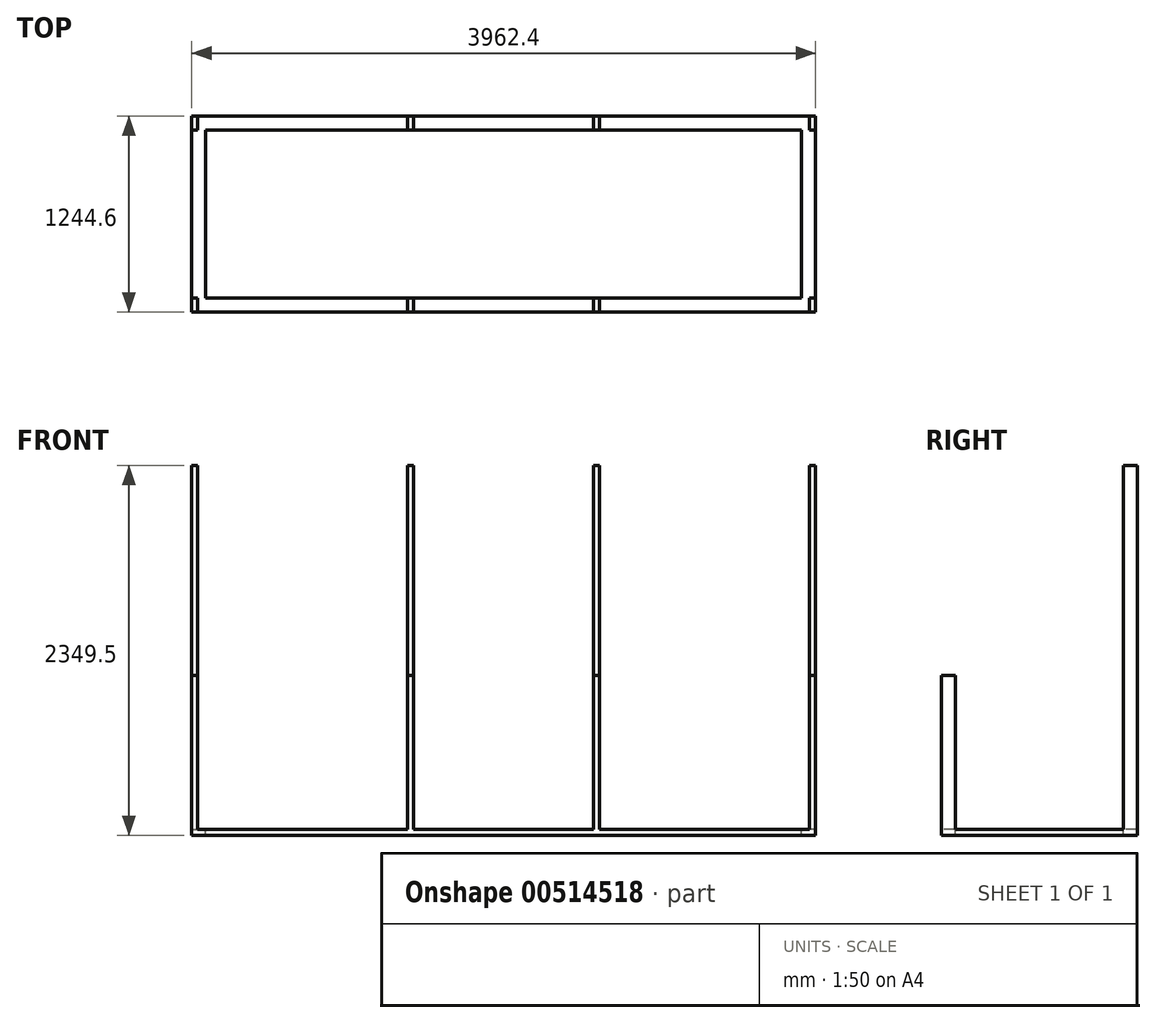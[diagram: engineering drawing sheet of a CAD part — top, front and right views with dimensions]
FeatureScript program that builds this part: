
annotation { "Feature Type Name" : "Feature", "Feature Type Description" : "" }
export const myFeature = defineFeature(function(context is Context, id is Id, definition is map)
    precondition{}
    {
        {
            var Q0;
            Q0=qCreatedBy(makeId("Front.planeOp"),FACE);
            var sketch = newSketch(context, id + "F0", { "sketchPlane" : qUnion([Q0])});
            skLineSegment(sketch, "E0.bottom", {"start": v(0, 0) * mm, "end": v(3962.4, 0) * mm});
            skLineSegment(sketch, "E0.top", {"start": v(0, 38.1) * mm, "end": v(3962.4, 38.1) * mm});
            skLineSegment(sketch, "E0.left", {"start": v(0, 0) * mm, "end": v(0, 38.1) * mm});
            skLineSegment(sketch, "E0.right", {"start": v(3962.4, 0) * mm, "end": v(3962.4, 38.1) * mm});
            skSolve(sketch);
        }
        {
            var Q0;
            Q0=makeQuery(id+"F0.imprint","IMPRINT",FACE,{"disambiguationData":[TD([[makeQuery(id+"F0.imprint","IMPRINT",EDGE,{"derivedFrom":sQuery(id+"F0.wireOp",EDGE,"E0.bottom")}),1.0]])]});
            extrude(context, id + "F1", {"entities" : qUnion([Q0]), "depth" : 88.9 * mm, "offsetDistance" : 25.4 * mm});
        }
        {
            var Q0;
            Q0=makeQuery(id+"F1.opExtrude","SWEPT_FACE",FACE,{"disambiguationData":[OSD([sQuery(id+"F0.wireOp",EDGE,"E0.top")])]});
            var sketch = newSketch(context, id + "F2", { "sketchPlane" : qUnion([Q0])});
            skLineSegment(sketch, "E1.bottom", {"start": v(0, 0) * mm, "end": v(38.1, 0) * mm});
            skLineSegment(sketch, "E1.top", {"start": v(0, -88.9) * mm, "end": v(38.1, -88.9) * mm});
            skLineSegment(sketch, "E1.left", {"start": v(0, 0) * mm, "end": v(0, -88.9) * mm});
            skLineSegment(sketch, "E1.right", {"start": v(38.1, 0) * mm, "end": v(38.1, -88.9) * mm});
            skLineSegment(sketch, "E2.bottom", {"start": v(3962.4, 0) * mm, "end": v(3924.3, 0) * mm});
            skLineSegment(sketch, "E2.top", {"start": v(3962.4, -88.9) * mm, "end": v(3924.3, -88.9) * mm});
            skLineSegment(sketch, "E2.left", {"start": v(3962.4, 0) * mm, "end": v(3962.4, -88.9) * mm});
            skLineSegment(sketch, "E2.right", {"start": v(3924.3, 0) * mm, "end": v(3924.3, -88.9) * mm});
            skLineSegment(sketch, "E3.bottom", {"start": v(2590.8, 0) * mm, "end": v(2552.7, 0) * mm});
            skLineSegment(sketch, "E3.top", {"start": v(2590.8, -88.9) * mm, "end": v(2552.7, -88.9) * mm});
            skLineSegment(sketch, "E3.left", {"start": v(2590.8, 0) * mm, "end": v(2590.8, -88.9) * mm});
            skLineSegment(sketch, "E3.right", {"start": v(2552.7, 0) * mm, "end": v(2552.7, -88.9) * mm});
            skLineSegment(sketch, "E4.bottom", {"start": v(1371.6, 0) * mm, "end": v(1409.7, 0) * mm});
            skLineSegment(sketch, "E4.top", {"start": v(1371.6, -88.9) * mm, "end": v(1409.7, -88.9) * mm});
            skLineSegment(sketch, "E4.left", {"start": v(1371.6, 0) * mm, "end": v(1371.6, -88.9) * mm});
            skLineSegment(sketch, "E4.right", {"start": v(1409.7, 0) * mm, "end": v(1409.7, -88.9) * mm});
            skSolve(sketch);
        }
        {
            var Q0;
            Q0=makeQuery(id+"F2.imprint","IMPRINT",FACE,{"disambiguationData":[TD([[makeQuery(id+"F2.imprint","IMPRINT",EDGE,{"derivedFrom":sQuery(id+"F2.wireOp",EDGE,"E1.bottom")}),-1.0]])]});
            var Q1;
            Q1=makeQuery(id+"F2.imprint","IMPRINT",FACE,{"disambiguationData":[TD([[makeQuery(id+"F2.imprint","IMPRINT",EDGE,{"derivedFrom":sQuery(id+"F2.wireOp",EDGE,"E4.bottom")}),-1.0]])]});
            var Q2;
            Q2=makeQuery(id+"F2.imprint","IMPRINT",FACE,{"disambiguationData":[TD([[makeQuery(id+"F2.imprint","IMPRINT",EDGE,{"derivedFrom":sQuery(id+"F2.wireOp",EDGE,"E3.bottom")}),-1.0]])]});
            var Q3;
            Q3=makeQuery(id+"F2.imprint","IMPRINT",FACE,{"disambiguationData":[TD([[makeQuery(id+"F2.imprint","IMPRINT",EDGE,{"derivedFrom":sQuery(id+"F2.wireOp",EDGE,"E2.bottom")}),-1.0]])]});
            extrude(context, id + "F3", {"entities" : qUnion([Q0, Q1, Q2, Q3]), "operationType" : NewBodyOperationType.ADD, "depth" : 977.9 * mm, "offsetDistance" : 25.4 * mm});
        }
        {
            var Q0;
            Q0=makeQuery(id+"F3.boolean.opBoolean","MERGE",FACE,{"derivedFrom":[makeQuery(id+"F1.opExtrude","CAP_FACE",FACE,{"disambiguationData":[OSD([sQuery(id+"F0.wireOp",EDGE,"E0.bottom"),sQuery(id+"F0.wireOp",EDGE,"E0.top"),sQuery(id+"F0.wireOp",EDGE,"E0.left"),sQuery(id+"F0.wireOp",EDGE,"E0.right")])],"isStart":true}),makeQuery(id+"F3.opExtrude","SWEPT_FACE",FACE,{"disambiguationData":[OSD([sQuery(id+"F2.wireOp",EDGE,"E1.bottom")])]}),makeQuery(id+"F3.opExtrude","SWEPT_FACE",FACE,{"disambiguationData":[OSD([sQuery(id+"F2.wireOp",EDGE,"E2.bottom")])]}),makeQuery(id+"F3.opExtrude","SWEPT_FACE",FACE,{"disambiguationData":[OSD([sQuery(id+"F2.wireOp",EDGE,"E3.bottom")])]}),makeQuery(id+"F3.opExtrude","SWEPT_FACE",FACE,{"disambiguationData":[OSD([sQuery(id+"F2.wireOp",EDGE,"E4.bottom")])]})]});
            var sketch = newSketch(context, id + "F4", { "sketchPlane" : qUnion([Q0])});
            skLineSegment(sketch, "E5.bottom", {"start": v(-3962.4, 0) * mm, "end": v(-3873.5, 0) * mm});
            skLineSegment(sketch, "E5.top", {"start": v(-3962.4, 38.1) * mm, "end": v(-3873.5, 38.1) * mm});
            skLineSegment(sketch, "E5.left", {"start": v(-3962.4, 0) * mm, "end": v(-3962.4, 38.1) * mm});
            skLineSegment(sketch, "E5.right", {"start": v(-3873.5, 0) * mm, "end": v(-3873.5, 38.1) * mm});
            skLineSegment(sketch, "E6.bottom", {"start": v(0, 0) * mm, "end": v(-88.9, 0) * mm});
            skLineSegment(sketch, "E6.top", {"start": v(0, 38.1) * mm, "end": v(-88.9, 38.1) * mm});
            skLineSegment(sketch, "E6.left", {"start": v(0, 0) * mm, "end": v(0, 38.1) * mm});
            skLineSegment(sketch, "E6.right", {"start": v(-88.9, 0) * mm, "end": v(-88.9, 38.1) * mm});
            skSolve(sketch);
        }
        {
            var Q0;
            Q0=makeQuery(id+"F4.imprint","IMPRINT",FACE,{"disambiguationData":[TD([[makeQuery(id+"F4.imprint","IMPRINT",EDGE,{"derivedFrom":sQuery(id+"F4.wireOp",EDGE,"E6.bottom")}),-1.0]])]});
            var Q1;
            Q1=makeQuery(id+"F4.imprint","IMPRINT",FACE,{"disambiguationData":[TD([[makeQuery(id+"F4.imprint","IMPRINT",EDGE,{"derivedFrom":sQuery(id+"F4.wireOp",EDGE,"E5.bottom")}),-1.0]])]});
            extrude(context, id + "F5", {"entities" : qUnion([Q0, Q1]), "operationType" : NewBodyOperationType.ADD, "depth" : 1066.8 * mm, "offsetDistance" : 25.4 * mm});
        }
        {
            var Q0;
            {var subQ3=sQuery(id+"F0.wireOp",EDGE,"E0.top");var subQ4=sQuery(id+"F2.wireOp",EDGE,"E4.bottom");var subQ6=sQuery(id+"F0.wireOp",EDGE,"E0.bottom");var subQ7=sQuery(id+"F2.wireOp",EDGE,"E3.bottom");Q0=makeQuery(id+"F5.boolean.opBoolean","SPLIT",FACE,{"disambiguationData":[TD([makeQuery(id+"F1.opExtrude","SWEPT_FACE",FACE,{"disambiguationData":[OSD([subQ6])]})])],"derivedFrom":makeQuery(id+"F3.boolean.opBoolean","MERGE",FACE,{"derivedFrom":[makeQuery(id+"F1.opExtrude","CAP_FACE",FACE,{"disambiguationData":[OSD([subQ6,subQ3,sQuery(id+"F0.wireOp",EDGE,"E0.left"),sQuery(id+"F0.wireOp",EDGE,"E0.right")])],"isStart":true}),makeQuery(id+"F3.opExtrude","SWEPT_FACE",FACE,{"disambiguationData":[OSD([sQuery(id+"F2.wireOp",EDGE,"E1.bottom")])]}),makeQuery(id+"F3.opExtrude","SWEPT_FACE",FACE,{"disambiguationData":[OSD([sQuery(id+"F2.wireOp",EDGE,"E2.bottom")])]}),makeQuery(id+"F3.opExtrude","SWEPT_FACE",FACE,{"disambiguationData":[OSD([subQ7])]}),makeQuery(id+"F3.opExtrude","SWEPT_FACE",FACE,{"disambiguationData":[OSD([subQ4])]})]})});}
            cPlane(context, id + "F6", {"entities" : qUnion([Q0]), "cplaneType" : CPlaneType.OFFSET, "offset" : 1066.8 * mm, "width" : 152.4 * mm, "height" : 152.4 * mm});
        }
        {
            var Q0;
            Q0=qCreatedBy(id+"F6.planeOp",FACE);
            var sketch = newSketch(context, id + "F7", { "sketchPlane" : qUnion([Q0])});
            skLineSegment(sketch, "E7.0", {"start": v(-3962.4, 0) * mm, "end": v(-3962.4, 38.1) * mm});
            skLineSegment(sketch, "E8.bottom", {"start": v(-3962.4, 0) * mm, "end": v(0, 0) * mm});
            skLineSegment(sketch, "E8.top", {"start": v(-3962.4, 38.1) * mm, "end": v(0, 38.1) * mm});
            skLineSegment(sketch, "E8.right", {"start": v(0, 0) * mm, "end": v(0, 38.1) * mm});
            skSolve(sketch);
        }
        {
            var Q0;
            Q0=makeQuery(id+"F7.imprint","IMPRINT",FACE,{"disambiguationData":[TD([[makeQuery(id+"F7.imprint","IMPRINT",EDGE,{"derivedFrom":sQuery(id+"F7.wireOp",EDGE,"E8.bottom")}),1.0]])]});
            extrude(context, id + "F8", {"entities" : qUnion([Q0]), "operationType" : NewBodyOperationType.ADD, "depth" : 88.9 * mm, "offsetDistance" : 25.4 * mm});
        }
        {
            var Q0;
            {var subQ7=sQuery(id+"F0.wireOp",EDGE,"E0.top");var subQ14=makeQuery(id+"F1.opExtrude","SWEPT_FACE",FACE,{"disambiguationData":[OSD([subQ7])]});Q0=makeQuery(id+"F8.boolean.opBoolean","MERGE",FACE,{"derivedFrom":[makeQuery(id+"F5.boolean.opBoolean","MERGE",FACE,{"derivedFrom":[makeQuery(id+"F3.boolean.opBoolean","SPLIT",FACE,{"disambiguationData":[TD([makeQuery(id+"F3.opExtrude","SWEPT_FACE",FACE,{"disambiguationData":[OSD([sQuery(id+"F2.wireOp",EDGE,"E1.right")])]})])],"derivedFrom":subQ14}),makeQuery(id+"F5.opExtrude","SWEPT_FACE",FACE,{"disambiguationData":[OSD([sQuery(id+"F4.wireOp",EDGE,"E6.top")])]})]}),makeQuery(id+"F5.boolean.opBoolean","MERGE",FACE,{"derivedFrom":[makeQuery(id+"F3.boolean.opBoolean","SPLIT",FACE,{"disambiguationData":[TD([makeQuery(id+"F3.opExtrude","SWEPT_FACE",FACE,{"disambiguationData":[OSD([sQuery(id+"F2.wireOp",EDGE,"E2.right")])]})])],"derivedFrom":subQ14}),makeQuery(id+"F5.opExtrude","SWEPT_FACE",FACE,{"disambiguationData":[OSD([sQuery(id+"F4.wireOp",EDGE,"E5.top")])]})]}),makeQuery(id+"F8.opExtrude","SWEPT_FACE",FACE,{"disambiguationData":[OSD([sQuery(id+"F7.wireOp",EDGE,"E8.top")])]})]});}
            var sketch = newSketch(context, id + "F9", { "sketchPlane" : qUnion([Q0])});
            skLineSegment(sketch, "E9.bottom", {"start": v(0, 1155.7) * mm, "end": v(38.1, 1155.7) * mm});
            skLineSegment(sketch, "E9.top", {"start": v(0, 1066.8) * mm, "end": v(38.1, 1066.8) * mm});
            skLineSegment(sketch, "E9.left", {"start": v(0, 1155.7) * mm, "end": v(0, 1066.8) * mm});
            skLineSegment(sketch, "E9.right", {"start": v(38.1, 1155.7) * mm, "end": v(38.1, 1066.8) * mm});
            skLineSegment(sketch, "E10.bottom", {"start": v(1371.6, 1155.7) * mm, "end": v(1409.7, 1155.7) * mm});
            skLineSegment(sketch, "E10.top", {"start": v(1371.6, 1066.8) * mm, "end": v(1409.7, 1066.8) * mm});
            skLineSegment(sketch, "E10.left", {"start": v(1371.6, 1155.7) * mm, "end": v(1371.6, 1066.8) * mm});
            skLineSegment(sketch, "E10.right", {"start": v(1409.7, 1155.7) * mm, "end": v(1409.7, 1066.8) * mm});
            skLineSegment(sketch, "E11.bottom", {"start": v(2552.7, 1066.8) * mm, "end": v(2590.8, 1066.8) * mm});
            skLineSegment(sketch, "E11.top", {"start": v(2552.7, 1155.7) * mm, "end": v(2590.8, 1155.7) * mm});
            skLineSegment(sketch, "E11.left", {"start": v(2552.7, 1066.8) * mm, "end": v(2552.7, 1155.7) * mm});
            skLineSegment(sketch, "E11.right", {"start": v(2590.8, 1066.8) * mm, "end": v(2590.8, 1155.7) * mm});
            skLineSegment(sketch, "E12.bottom", {"start": v(3962.4, 1155.7) * mm, "end": v(3924.3, 1155.7) * mm});
            skLineSegment(sketch, "E12.top", {"start": v(3962.4, 1066.8) * mm, "end": v(3924.3, 1066.8) * mm});
            skLineSegment(sketch, "E12.left", {"start": v(3962.4, 1155.7) * mm, "end": v(3962.4, 1066.8) * mm});
            skLineSegment(sketch, "E12.right", {"start": v(3924.3, 1155.7) * mm, "end": v(3924.3, 1066.8) * mm});
            skSolve(sketch);
        }
        {
            var Q0;
            Q0=makeQuery(id+"F9.imprint","IMPRINT",FACE,{"disambiguationData":[TD([[makeQuery(id+"F9.imprint","IMPRINT",EDGE,{"derivedFrom":sQuery(id+"F9.wireOp",EDGE,"E12.bottom")}),1.0]])]});
            var Q1;
            Q1=makeQuery(id+"F9.imprint","IMPRINT",FACE,{"disambiguationData":[TD([[makeQuery(id+"F9.imprint","IMPRINT",EDGE,{"derivedFrom":sQuery(id+"F9.wireOp",EDGE,"E11.bottom")}),-1.0]])]});
            var Q2;
            Q2=makeQuery(id+"F9.imprint","IMPRINT",FACE,{"disambiguationData":[TD([[makeQuery(id+"F9.imprint","IMPRINT",EDGE,{"derivedFrom":sQuery(id+"F9.wireOp",EDGE,"E10.bottom")}),1.0]])]});
            var Q3;
            Q3=makeQuery(id+"F9.imprint","IMPRINT",FACE,{"disambiguationData":[TD([[makeQuery(id+"F9.imprint","IMPRINT",EDGE,{"derivedFrom":sQuery(id+"F9.wireOp",EDGE,"E9.bottom")}),1.0]])]});
            extrude(context, id + "F10", {"entities" : qUnion([Q0, Q1, Q2, Q3]), "operationType" : NewBodyOperationType.ADD, "depth" : 2311.4 * mm, "offsetDistance" : 25.4 * mm});
        }
    });
